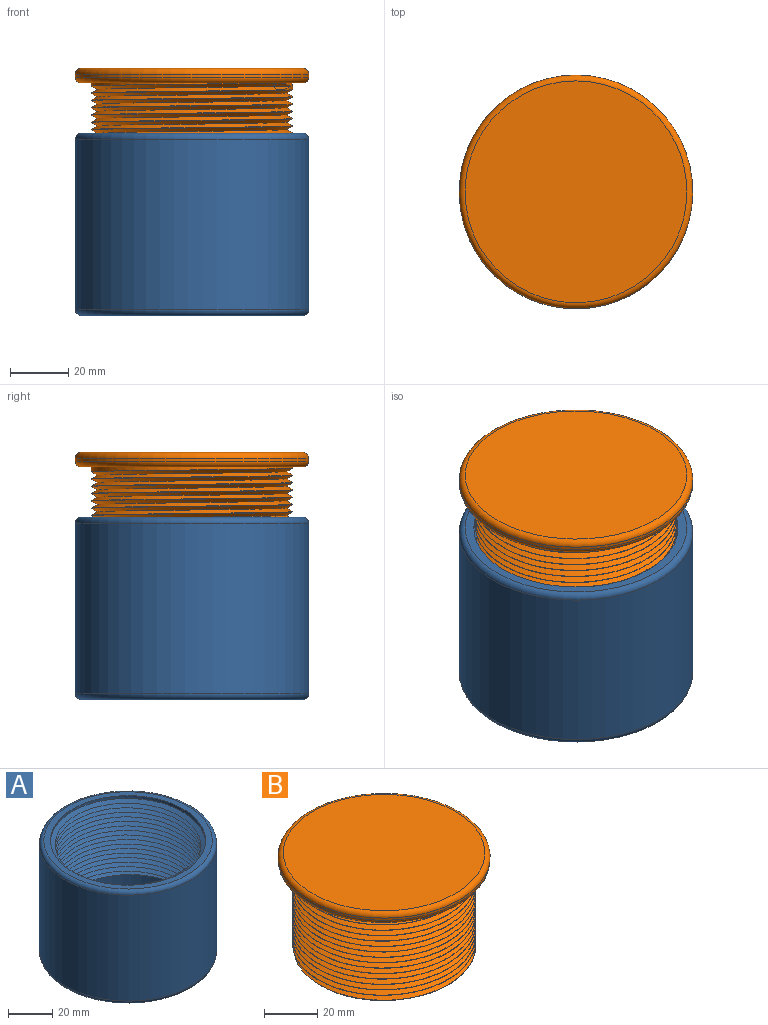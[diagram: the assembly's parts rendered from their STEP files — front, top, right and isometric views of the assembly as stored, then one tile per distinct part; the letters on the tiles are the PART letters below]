
ASSEMBLY  parts=2 mates=1
PART A: 30 faces, bbox 88.7x88.7x64.6 mm
  f0: cylinder r=35mm len=70mm, axis (0,0,1), area 1765.2mm2, adj f16,f21,f22,f25,f27
  f1: cylinder r=35mm len=70mm, axis (0,0,1), area 117.4mm2, adj f2,f17,f20,f21,f22,f23,f24
  f2: cylinder r=35mm len=70mm, axis (0,0,1), area 21.9mm2, adj f1,f3,f21,f22
  f3: cylinder r=35mm len=70mm, axis (0,0,1), area 22mm2, adj f2,f4,f21,f22
  f4: cylinder r=35mm len=70mm, axis (0,0,1), area 22mm2, adj f3,f5,f21,f22
  f5: cylinder r=35mm len=70mm, axis (0,0,1), area 22mm2, adj f4,f6,f21,f22
  f6: cylinder r=35mm len=70mm, axis (0,0,1), area 22mm2, adj f5,f7,f21,f22
  f7: cylinder r=35mm len=70mm, axis (0,0,1), area 22mm2, adj f6,f8,f21,f22
  f8: cylinder r=35mm len=70mm, axis (0,0,1), area 22mm2, adj f7,f9,f21,f22
  f9: cylinder r=35mm len=70mm, axis (0,0,1), area 22mm2, adj f8,f10,f21,f22
  f10: cylinder r=35mm len=70mm, axis (0,0,1), area 22mm2, adj f9,f11,f21,f22
  f11: cylinder r=35mm len=70mm, axis (0,0,1), area 21.9mm2, adj f10,f12,f21,f22
  f12: cylinder r=35mm len=70mm, axis (0,0,1), area 22mm2, adj f11,f13,f21,f22
  f13: cylinder r=35mm len=70mm, axis (0,0,1), area 22mm2, adj f12,f14,f21,f22
  f14: cylinder r=35mm len=70mm, axis (0,0,1), area 22mm2, adj f13,f15,f21,f22
  f15: cylinder r=35mm len=70mm, axis (0,0,1), area 22mm2, adj f14,f16,f21,f22
  f16: cylinder r=35mm len=70mm, axis (0,0,1), area 22mm2, adj f0,f15,f21,f22
  f17: cylinder r=35mm len=70mm, axis (0,0,1), area 154.6mm2, adj f1,f20,f21
  f18: cylinder r=40mm len=80mm, axis (0,0,1), area 14702.7mm2, adj f28,f29
  f19: plane 76x76mm, normal (0,0,-1), area 4536.5mm2, adj f29
  f20: plane 76x76mm, normal (0,0,1), area 688mm2, adj f1,f17,f28
  f21: bspline ~80.83x70mm, area 8536.3mm2, adj f0,f1,f2,f3,f4,f5,f6,f7
  f22: bspline ~80.83x70mm, area 8338.4mm2, adj f0,f1,f2,f3,f4,f5,f6,f7
  f23: plane 11.88x2.08mm, normal (0,0.5,0.87), area 19.1mm2, adj f1,f21,f24
  f24: plane 11.88x2.08mm, normal (0,0.5,-0.87), area 19.1mm2, adj f1,f22,f23
  f25: plane 72.14x72.14mm, normal (0,0,-1), area 215mm2, adj f0,f21,f22
  f26: plane 66x66mm, normal (0,0,1), area 3421.2mm2, adj f27
  f27: torus R=33mm, axis (0,0,1), area 676.5mm2, adj f0,f26
  f28: torus R=38mm, axis (0,0,1), area 775.2mm2, adj f18,f20
  f29: torus R=38mm, axis (0,0,1), area 775.2mm2, adj f18,f19
PART B: 12 faces, bbox 87.3x87.3x47.3 mm
  f0: cylinder r=40mm len=80mm, axis (0,0,-1), area 251.3mm2, adj f10,f11
  f1: plane 76x76mm, normal (0,0,1), area 4536.5mm2, adj f11
  f2: plane 76x76mm, normal (0,0,-1), area 797.2mm2, adj f3,f10
  f3: cylinder r=34.5mm len=69mm, axis (0,0,1), area -412.8mm2, adj f2,f5,f6,f7,f8,f9
  f4: plane 67.31x66.53mm, normal (0,0,-1), area 3446.7mm2, adj f5,f6,f7
  f5: cone r=34.5mm half-angle=45deg, axis (0,0,1), area 113.6mm2, adj f3,f4,f6,f7
  f6: bspline ~79.67x69mm, area 7880.1mm2, adj f3,f4,f5,f7,f8
  f7: bspline ~79.67x69mm, area 7634.5mm2, adj f3,f4,f5,f6,f9
  f8: plane 12.39x2.67mm, normal (0,0.5,-0.87), area 19mm2, adj f3,f6,f9
  f9: plane 12.39x2.67mm, normal (0,0.5,0.87), area 19mm2, adj f3,f7,f8
  f10: torus R=38mm, axis (0,0,1), area 775.2mm2, adj f0,f2
  f11: torus R=38mm, axis (0,0,1), area 775.2mm2, adj f0,f1
PLACE A t=(-34.88,38.76,81.94)mm
PLACE B rot(axis=(0,0,-1),121.7deg) t=(-34.88,38.76,49.15)mm
MATE cylindrical A.f18 <-> B.f3  axis (0,0,1) through (-34.88,38.76,0.69)mm
